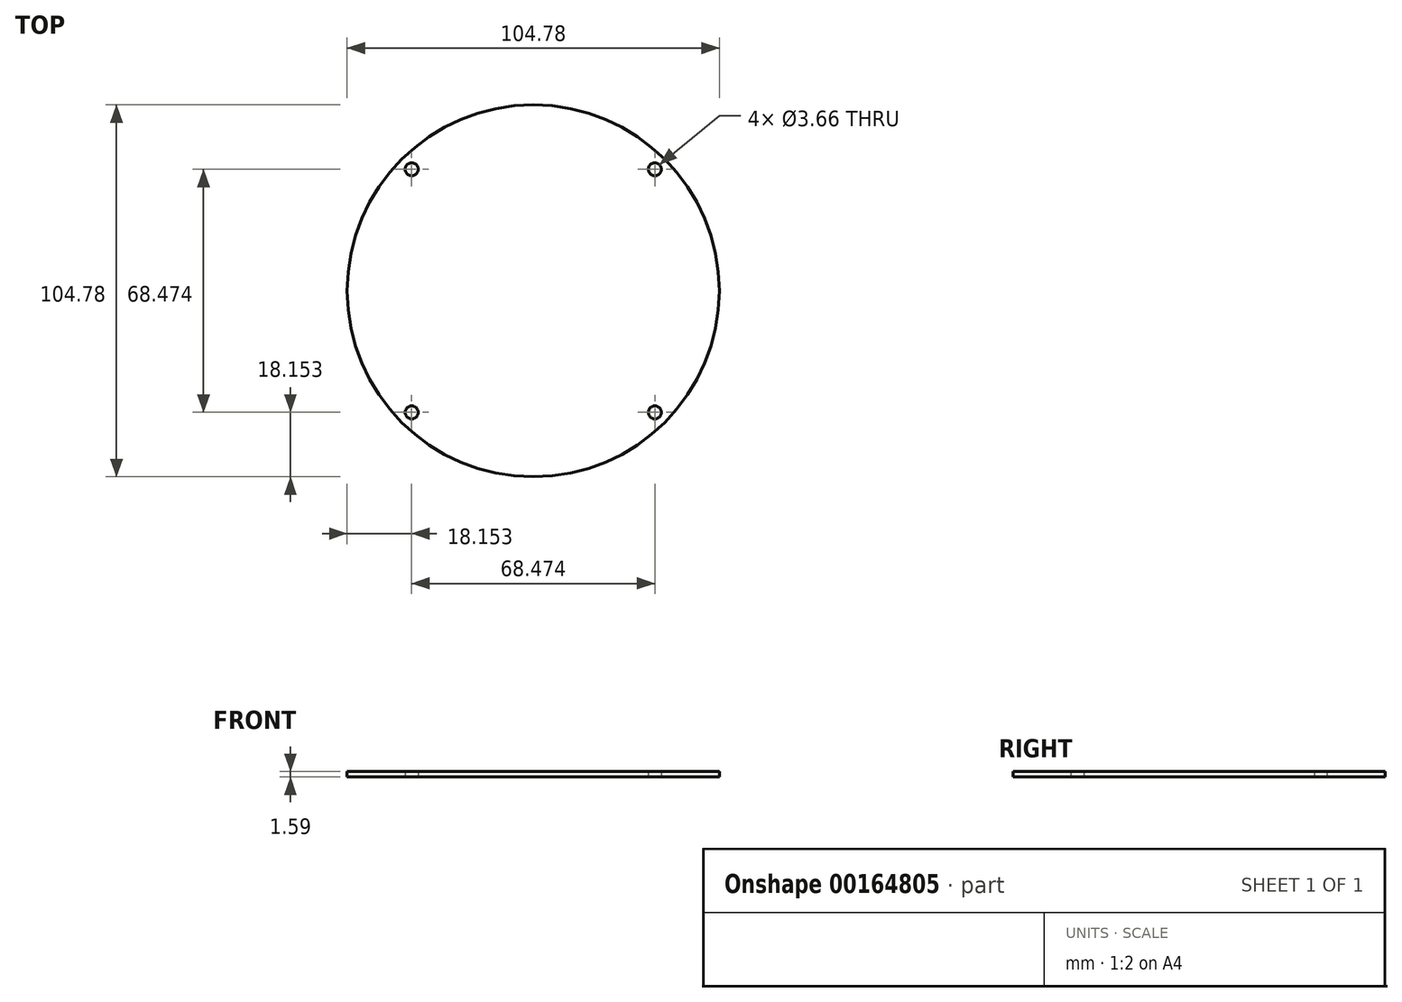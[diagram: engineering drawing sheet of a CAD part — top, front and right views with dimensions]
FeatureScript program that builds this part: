
annotation { "Feature Type Name" : "Feature", "Feature Type Description" : "" }
export const myFeature = defineFeature(function(context is Context, id is Id, definition is map)
    precondition{}
    {
        {
            var Q0;
            Q0=qCreatedBy(makeId("Top.planeOp"),FACE);
            var sketch = newSketch(context, id + "F0", { "sketchPlane" : qUnion([Q0])});
            skCircle(sketch, "E0", {"center": v(0, 0) * mm, "radius": 52.39 * mm});
            skLineSegment(sketch, "E1.bottom", {"start": v(34.24, 34.24) * mm, "end": v(-34.24, 34.24) * mm, "construction": true});
            skLineSegment(sketch, "E1.top", {"start": v(34.24, -34.24) * mm, "end": v(-34.24, -34.24) * mm, "construction": true});
            skLineSegment(sketch, "E1.left", {"start": v(34.24, 34.24) * mm, "end": v(34.24, -34.24) * mm, "construction": true});
            skLineSegment(sketch, "E1.right", {"start": v(-34.24, 34.24) * mm, "end": v(-34.24, -34.24) * mm, "construction": true});
            skCircle(sketch, "E2", {"center": v(34.24, 34.24) * mm, "radius": 3.97 * mm, "construction": true});
            skCircle(sketch, "E3", {"center": v(-34.24, 34.24) * mm, "radius": 1.83 * mm});
            skCircle(sketch, "E4", {"center": v(34.24, 34.24) * mm, "radius": 1.83 * mm});
            skCircle(sketch, "E5", {"center": v(34.24, -34.24) * mm, "radius": 1.83 * mm});
            skCircle(sketch, "E6", {"center": v(-34.24, -34.24) * mm, "radius": 1.83 * mm});
            skSolve(sketch);
        }
        {
            var Q0;
            Q0 = qSketchRegion(id + "F0", true);
            extrude(context, id + "F1", {"entities" : qUnion([Q0]), "depth" : 1.59 * mm});
        }
    });
